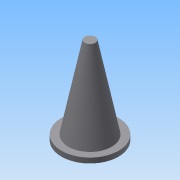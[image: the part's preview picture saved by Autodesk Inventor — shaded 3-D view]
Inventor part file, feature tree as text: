
AUTODESK INVENTOR PART (.ipt)
format: ipt  version: 2015 SP1 (Build 190203100, 203)  size: 97,280 bytes
history: native  units: in
note: dims shown in document units (in); Inventor stores cm internally (conversion verified against a paired STEP export)
features: revolve x1, sketch x1
ambient origin geometry x8: Origin, YZ Plane, XZ Plane, XY Plane, X Axis, Y Axis, Z Axis, Center Point
bodies: Solid1 (feature_tree)
feature tree (2):
  revolve  "Revolution1"  [1 undecoded]
  sketch  "Sketch1"  dims[d0=0.7in d1=0.125in d2=0.17in d3=2.135in d5=90.0deg d6=0.13in]
note: 1 required parameter value undecoded (feature->parameter linkage not recoverable at this tier; creation-order binding heuristic only, values carry confidence <= 0.55)
